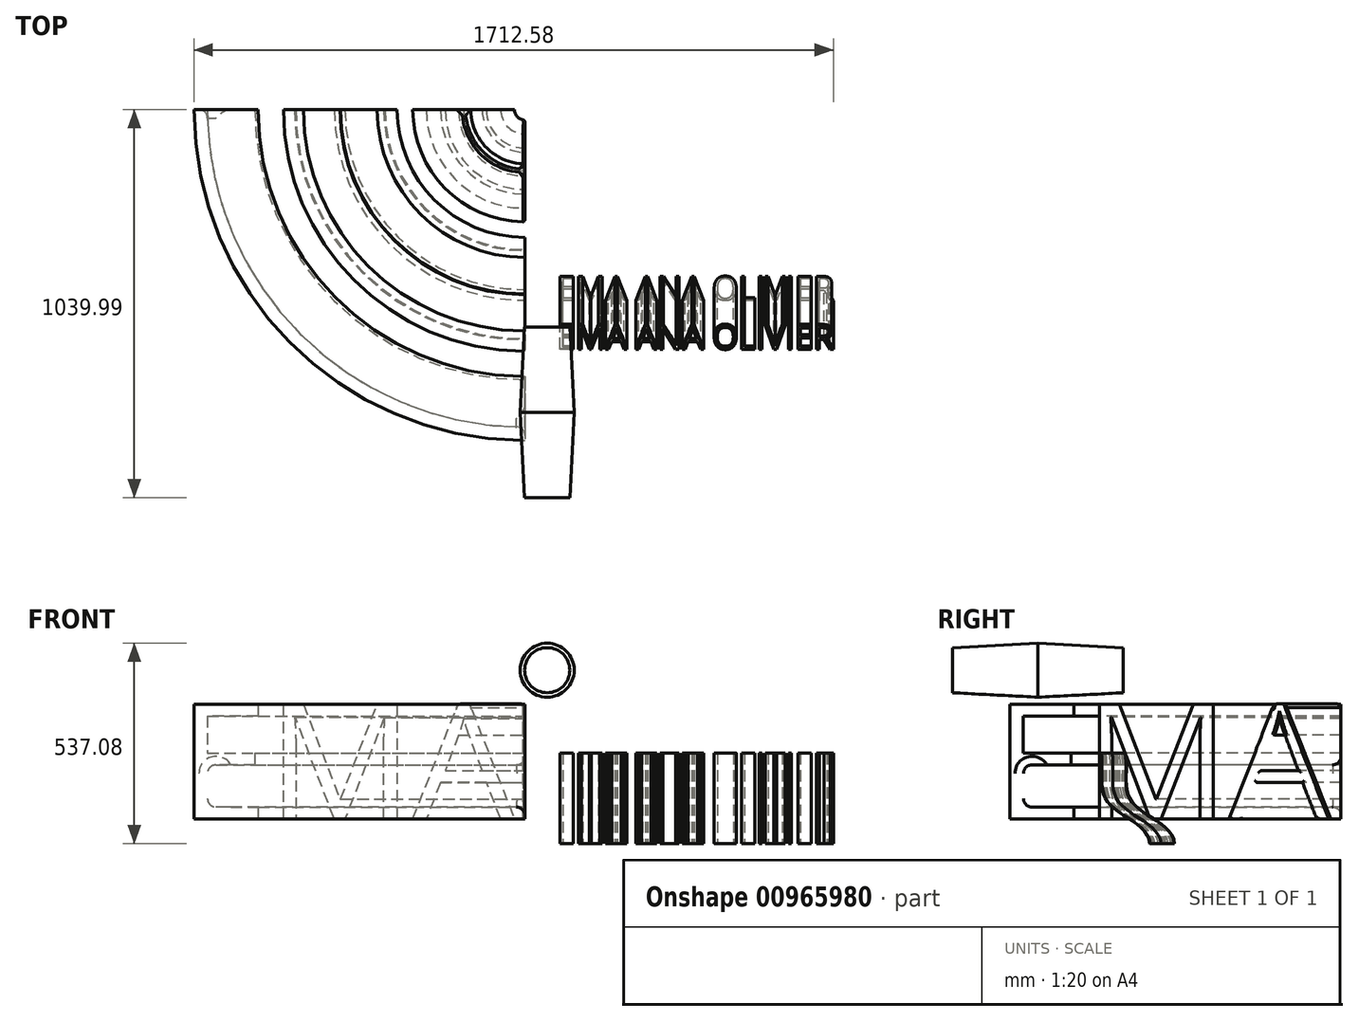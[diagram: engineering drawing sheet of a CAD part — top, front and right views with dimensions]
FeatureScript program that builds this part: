
annotation { "Feature Type Name" : "Feature", "Feature Type Description" : "" }
export const myFeature = defineFeature(function(context is Context, id is Id, definition is map)
    precondition{}
    {
        {
            var Q0;
            Q0=qCreatedBy(makeId("Top.planeOp"),FACE);
            var sketch = newSketch(context, id + "F0", { "sketchPlane" : qUnion([Q0])});
            skText(sketch, "E0", { "text": "EMA ANA OLIVIER", "fontName": "OpenSans-Regular.ttf"});
            const initialGuessF0  = {"E0": [0.085, 0.16904, 1, 0, 0.06476]};
            skSetInitialGuess(sketch, initialGuessF0);
            skSolve(sketch);
        }
        {
            var Q0;
            Q0=qCreatedBy(makeId("Right.planeOp"),FACE);
            var sketch = newSketch(context, id + "F1", { "sketchPlane" : qUnion([Q0])});
            skFitSpline(sketch, "E1", {"points": [v(320.48, -181.57) * mm, v(337.23, -311.19) * mm, v(451.74, -424.24) * mm], "startDerivative": vector(52.98, -260) * mm, "endDerivative": vector(15.35, -294.18) * mm});
            skSolve(sketch);
        }
        {
            var Q0;
            Q0 = qSketchRegion(id + "F0", true);
            var Q1;
            Q1 = qBodyType(qCreatedBy(id + "F1" ,EDGE), BodyType.WIRE);
            sweep(context, id + "F2", {"profiles" : qUnion([Q0]), "path" : qUnion([Q1]), "keepProfileOrientation" : true});
        }
        {
            var Q0;
            Q0=qCreatedBy(makeId("Right.planeOp"),FACE);
            var sketch = newSketch(context, id + "F3", { "sketchPlane" : qUnion([Q0])});
            skText(sketch, "E2", { "text": "EMA", "fontName": "OpenSans-Regular.ttf"});
            const initialGuessF3  = {"E2": [-0.11743, -0.17676, 1, 0, 0.3101]};
            skSetInitialGuess(sketch, initialGuessF3);
            skSolve(sketch);
        }
        {
            var Q0;
            Q0 = qSketchRegion(id + "F3", true);
            var Q1;
            Q1=sQuery(id+"F3.wireOp",EDGE,"E2.sketch_text.right");
            revolve(context, id + "F4", {"surfaceOperationType" : NewSurfaceOperationType.NEW, "entities" : qUnion([Q0]), "axis" : qUnion([Q1]), "revolveType" : RevolveType.ONE_DIRECTION, "oppositeDirection" : true, "angle" : 90 * degree});
        }
        {
            var Q0;
            Q0=qCreatedBy(makeId("Front.planeOp"),FACE);
            var sketch = newSketch(context, id + "F5", { "sketchPlane" : qUnion([Q0])});
            skLineSegment(sketch, "E3", {"start": v(371.5, 1266.27) * mm, "end": v(636.98, 1419.54) * mm});
            skLineSegment(sketch, "E4", {"start": v(974.24, 980) * mm, "end": v(371.5, 377.27) * mm});
            skLineSegment(sketch, "E5", {"start": v(371.5, 377.27) * mm, "end": v(371.5, 1266.27) * mm});
            skArc(sketch, "E6.filletArc", {"start": v(974.24, 980) * mm, "mid": v(998.34, 1347.66) * mm, "end": v(636.98, 1419.54) * mm});
            skSolve(sketch);
        }
        {
            var Q0;
            Q0 = qSketchRegion(id + "F5", true);
            extrude(context, id + "F6", {"entities" : qUnion([Q0]), "depth" : 635 * mm, "offsetDistance" : 25.4 * mm});
        }
        {
            var Q0;
            Q0=makeQuery(id+"F6.opExtrude","CAP_EDGE",EDGE,{"disambiguationData":[OSD([sQuery(id+"F5.wireOp",EDGE,"E6.filletArc")])],"isStart":false});
            var Q1;
            Q1=makeQuery(id+"F6.opExtrude","CAP_EDGE",EDGE,{"disambiguationData":[OSD([sQuery(id+"F5.wireOp",EDGE,"E3")])],"isStart":false});
            var Q2;
            Q2=makeQuery(id+"F6.opExtrude","CAP_EDGE",EDGE,{"disambiguationData":[OSD([sQuery(id+"F5.wireOp",EDGE,"E4")])],"isStart":false});
            var Q3;
            Q3=makeQuery(id+"F6.opExtrude","CAP_EDGE",EDGE,{"disambiguationData":[OSD([sQuery(id+"F5.wireOp",EDGE,"E4")])],"isStart":true});
            var Q4;
            Q4=makeQuery(id+"F6.opExtrude","CAP_EDGE",EDGE,{"disambiguationData":[OSD([sQuery(id+"F5.wireOp",EDGE,"E6.filletArc")])],"isStart":true});
            var Q5;
            Q5=makeQuery(id+"F6.opExtrude","CAP_EDGE",EDGE,{"disambiguationData":[OSD([sQuery(id+"F5.wireOp",EDGE,"E3")])],"isStart":true});
            var Q6;
            Q6=makeQuery(id+"FwXbTRWnGsTLsvv_31.1.F6.opExtrude","CAP_EDGE",EDGE,{"disambiguationData":[OSD([sQuery(id+"F5.wireOp",EDGE,"E3")])],"isStart":true});
            var Q7;
            Q7=makeQuery(id+"FwXbTRWnGsTLsvv_31.1.F6.opExtrude","CAP_EDGE",EDGE,{"disambiguationData":[OSD([sQuery(id+"F5.wireOp",EDGE,"E6.filletArc")])],"isStart":true});
            var Q8;
            Q8=makeQuery(id+"FwXbTRWnGsTLsvv_31.1.F6.opExtrude","CAP_EDGE",EDGE,{"disambiguationData":[OSD([sQuery(id+"F5.wireOp",EDGE,"E4")])],"isStart":true});
            var Q9;
            Q9=makeQuery(id+"FwXbTRWnGsTLsvv_31.1.F6.opExtrude","CAP_EDGE",EDGE,{"disambiguationData":[OSD([sQuery(id+"F5.wireOp",EDGE,"E4")])],"isStart":false});
            var Q10;
            Q10=makeQuery(id+"FwXbTRWnGsTLsvv_31.1.F6.opExtrude","CAP_EDGE",EDGE,{"disambiguationData":[OSD([sQuery(id+"F5.wireOp",EDGE,"E6.filletArc")])],"isStart":false});
            var Q11;
            Q11=makeQuery(id+"FwXbTRWnGsTLsvv_31.1.F6.opExtrude","CAP_EDGE",EDGE,{"disambiguationData":[OSD([sQuery(id+"F5.wireOp",EDGE,"E3")])],"isStart":false});
            fillet(context, id + "F7", {"entities" : qUnion([Q0, Q1, Q2, Q3, Q4, Q5, Q6, Q7, Q8, Q9, Q10, Q11]), "radius" : 254 * mm, "tangentPropagation" : true, "rho" : .2, "crossSection" : FilletCrossSection.CONIC, "allowEdgeOverflow" : false});
        }
        {
            var Q0;
            Q0=qCreatedBy(makeId("Front.planeOp"),FACE);
            var sketch = newSketch(context, id + "F8", { "sketchPlane" : qUnion([Q0])});
            skCircle(sketch, "E7", {"center": v(59.48, 222.02) * mm, "radius": 72.4 * mm});
            skSolve(sketch);
        }
        {
            var Q0;
            Q0 = qSketchRegion(id + "F8", true);
            extrude(context, id + "F9", {"entities" : qUnion([Q0]), "depth" : 228.6 * mm, "offsetDistance" : 25.4 * mm, "hasDraft" : true, "draftAngle" : 3 * degree, "draftPullDirection" : true, "hasSecondDirection" : true, "secondDirectionOppositeDirection" : true, "secondDirectionDepth" : 228.6 * mm, "hasSecondDirectionDraft" : true, "secondDirectionDraftAngle" : 3 * degree, "secondDirectionDraftPullDirection" : true});
        }
        {
            var Q0;
            Q0=makeQuery(id+"F6.opExtrude","SWEPT_BODY",BODY,{"disambiguationData":[OSD([sQuery(id+"F5.wireOp",EDGE,"E3"),sQuery(id+"F5.wireOp",EDGE,"E4"),sQuery(id+"F5.wireOp",EDGE,"E5"),sQuery(id+"F5.wireOp",EDGE,"E6.filletArc")])]});
            var Q1;
            Q1=makeQuery(id+"FwXbTRWnGsTLsvv_31.1.F6.opExtrude","SWEPT_BODY",BODY,{"disambiguationData":[OSD([sQuery(id+"F5.wireOp",EDGE,"E3"),sQuery(id+"F5.wireOp",EDGE,"E4"),sQuery(id+"F5.wireOp",EDGE,"E5"),sQuery(id+"F5.wireOp",EDGE,"E6.filletArc")])]});
            deleteBodies(context, id + "F10", {"entities" : qUnion([Q0, Q1])});
        }
        {
            var Q0;
            Q0=makeQuery(id+"F4.opRevolve","SWEPT_FACE",FACE,{"disambiguationData":[OSD([sQuery(id+"F3.wireOp",EDGE,"E2.sketch_text.stroke-35")])]});
            fillet(context, id + "F11", {"entities" : qUnion([Q0]), "radius" : 15.24 * mm, "rho" : .5, "crossSection" : FilletCrossSection.CONIC, "allowEdgeOverflow" : false});
        }
        {
            var Q0;
            Q0=makeQuery(id+"F4.opRevolve","CAP_FACE",FACE,{"disambiguationData":[OSD([sQuery(id+"F3.wireOp",EDGE,"E2.sketch_text.stroke-30"),sQuery(id+"F3.wireOp",EDGE,"E2.sketch_text.stroke-31"),sQuery(id+"F3.wireOp",EDGE,"E2.sketch_text.stroke-32"),sQuery(id+"F3.wireOp",EDGE,"E2.sketch_text.stroke-33"),sQuery(id+"F3.wireOp",EDGE,"E2.sketch_text.stroke-34"),sQuery(id+"F3.wireOp",EDGE,"E2.sketch_text.stroke-35"),sQuery(id+"F3.wireOp",EDGE,"E2.sketch_text.stroke-36"),sQuery(id+"F3.wireOp",EDGE,"E2.sketch_text.stroke-37"),sQuery(id+"F3.wireOp",EDGE,"E2.sketch_text.stroke-38"),sQuery(id+"F3.wireOp",EDGE,"E2.sketch_text.stroke-39"),sQuery(id+"F3.wireOp",EDGE,"E2.sketch_text.stroke-40"),sQuery(id+"F3.wireOp",EDGE,"E2.sketch_text.stroke-41"),sQuery(id+"F3.wireOp",EDGE,"E2.sketch_text.stroke-42")])],"isStart":true});
            fillet(context, id + "F12", {"entities" : qUnion([Q0]), "radius" : 5.08 * mm, "tangentPropagation" : true, "allowEdgeOverflow" : false});
        }
        {
            var Q0;
            Q0=makeQuery(id+"F4.opRevolve","SWEPT_FACE",FACE,{"disambiguationData":[OSD([sQuery(id+"F3.wireOp",EDGE,"E2.sketch_text.stroke-9")])]});
            fillet(context, id + "F13", {"entities" : qUnion([Q0]), "radius" : 22.86 * mm, "tangentPropagation" : true, "allowEdgeOverflow" : false});
        }
    });
